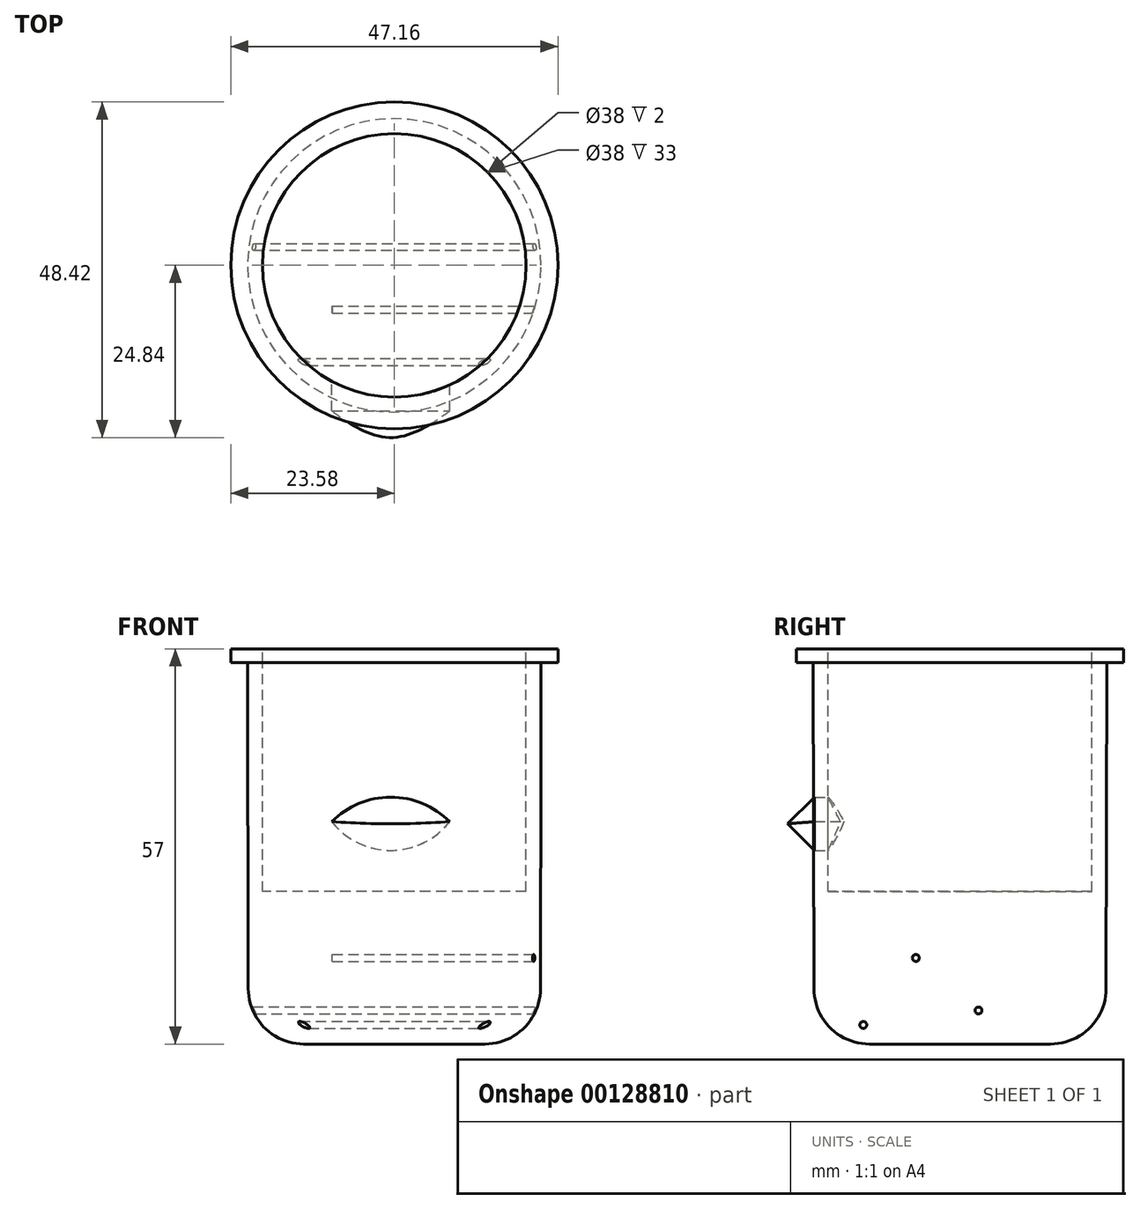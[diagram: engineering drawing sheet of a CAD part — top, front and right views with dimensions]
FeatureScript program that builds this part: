
annotation { "Feature Type Name" : "Feature", "Feature Type Description" : "" }
export const myFeature = defineFeature(function(context is Context, id is Id, definition is map)
    precondition{}
    {
        {
            var Q0;
            Q0=qCreatedBy(makeId("Top.planeOp"),FACE);
            cPlane(context, id + "F0", {"entities" : qUnion([Q0]), "cplaneType" : CPlaneType.OFFSET, "offset" : 55 * mm, "width" : 150 * mm, "height" : 150 * mm});
        }
        {
            var Q0;
            Q0=qCreatedBy(makeId("Top.planeOp"),FACE);
            var sketch = newSketch(context, id + "F1", { "sketchPlane" : qUnion([Q0])});
            skCircle(sketch, "E0", {"center": v(0, 0) * mm, "radius": 21.05 * mm});
            skSolve(sketch);
        }
        {
            var Q0;
            Q0=qCreatedBy(id+"F0.planeOp",FACE);
            var sketch = newSketch(context, id + "F2", { "sketchPlane" : qUnion([Q0])});
            skCircle(sketch, "E1", {"center": v(0, 0) * mm, "radius": 21.16 * mm});
            skSolve(sketch);
        }
        {
            var Q0;
            Q0 = qSketchRegion(id + "F1", true);
            var Q1;
            Q1 = qSketchRegion(id + "F2", true);
            loft(context, id + "F3", {"sheetProfilesArray" : [{ "sheetProfileEntities" : qUnion([Q0]) }, { "sheetProfileEntities" : qUnion([Q1]) }]});
        }
        {
            var Q0;
            Q0=makeQuery(id+"F3.opLoft","CAP_FACE",FACE,{"disambiguationData":[OSD([makeQuery(id+"F1.imprint","IMPRINT",FACE,{"disambiguationData":[TD([[makeQuery(id+"F1.imprint","IMPRINT",EDGE,{"derivedFrom":sQuery(id+"F1.wireOp",EDGE,"E0")}),1.0]])]})])],"isStart":true});
            fillet(context, id + "F4", {"entities" : qUnion([Q0]), "radius" : 8 * mm, "tangentPropagation" : true, "allowEdgeOverflow" : false});
        }
        {
            var Q0;
            Q0=qCreatedBy(makeId("Front.planeOp"),FACE);
            cPlane(context, id + "F5", {"entities" : qUnion([Q0]), "cplaneType" : CPlaneType.OFFSET, "offset" : 21 * mm, "width" : 150 * mm, "height" : 150 * mm});
        }
        {
            var Q0;
            Q0=qCreatedBy(id+"F5.planeOp",FACE);
            var sketch = newSketch(context, id + "F6", { "sketchPlane" : qUnion([Q0])});
            skLineSegment(sketch, "E2", {"start": v(0, 0) * mm, "end": v(0, 27.95) * mm});
            skArc(sketch, "E3", {"start": v(7.97, 32.08) * mm, "mid": v(-0.53, 35.62) * mm, "end": v(-9.03, 32.08) * mm});
            skArc(sketch, "E4", {"start": v(-9.03, 32.08) * mm, "mid": v(-0.53, 27.93) * mm, "end": v(7.97, 32.08) * mm});
            skSolve(sketch);
        }
        {
            var Q0;
            Q0 = qSketchRegion(id + "F6", true);
            extrude(context, id + "F7", {"entities" : qUnion([Q0]), "depth" : 10 * mm, "symmetric" : true});
        }
        {
            var Q0;
            Q0=makeQuery(id+"F7.opExtrude","CAP_EDGE",EDGE,{"disambiguationData":[OSD([sQuery(id+"F6.wireOp",EDGE,"E3")])],"isStart":false});
            chamfer(context, id + "F8", {"entities" : qUnion([Q0]), "chamferType" : ChamferType.TWO_OFFSETS, "width1" : 5 * mm, "oppositeDirection" : false, "width2" : 5 * mm, "tangentPropagation" : true});
        }
        {
            var Q0;
            Q0=makeQuery(id+"F7.opExtrude","CAP_EDGE",EDGE,{"disambiguationData":[OSD([sQuery(id+"F6.wireOp",EDGE,"E4")])],"isStart":false});
            chamfer(context, id + "F9", {"entities" : qUnion([Q0]), "width" : 5 * mm, "tangentPropagation" : true});
        }
        {
            var Q0;
            Q0=qCreatedBy(id+"F0.planeOp",FACE);
            var sketch = newSketch(context, id + "F10", { "sketchPlane" : qUnion([Q0])});
            skCircle(sketch, "E5", {"center": v(0, 0) * mm, "radius": 23.58 * mm});
            skSolve(sketch);
        }
        {
            var Q0;
            Q0 = qSketchRegion(id + "F10", true);
            extrude(context, id + "F11", {"entities" : qUnion([Q0]), "depth" : 2 * mm});
        }
        {
            var Q0;
            Q0=qCreatedBy(id+"F0.planeOp",FACE);
            cPlane(context, id + "F12", {"entities" : qUnion([Q0]), "cplaneType" : CPlaneType.OFFSET, "offset" : 2 * mm, "width" : 150 * mm, "height" : 150 * mm});
        }
        {
            var Q0;
            Q0=qCreatedBy(id+"F12.planeOp",FACE);
            var sketch = newSketch(context, id + "F13", { "sketchPlane" : qUnion([Q0])});
            skCircle(sketch, "E6", {"center": v(0, 0) * mm, "radius": 19 * mm});
            skSolve(sketch);
        }
        {
            var Q0;
            Q0 = qSketchRegion(id + "F13", true);
            extrude(context, id + "F14", {"entities" : qUnion([Q0]), "operationType" : NewBodyOperationType.REMOVE, "oppositeDirection" : true, "depth" : 35 * mm});
        }
        {
            var Q0;
            Q0=qCreatedBy(makeId("Right.planeOp"),FACE);
            cPlane(context, id + "F15", {"entities" : qUnion([Q0]), "cplaneType" : CPlaneType.OFFSET, "offset" : 21 * mm, "width" : 150 * mm, "height" : 150 * mm});
        }
        {
            var Q0;
            Q0=qCreatedBy(id+"F15.planeOp",FACE);
            var sketch = newSketch(context, id + "F16", { "sketchPlane" : qUnion([Q0])});
            skLineSegment(sketch, "E7", {"start": v(2.66, 0) * mm, "end": v(2.66, 4.84) * mm});
            skCircle(sketch, "E8", {"center": v(2.66, 4.84) * mm, "radius": 0.5 * mm});
            skSolve(sketch);
        }
        {
            var Q0;
            Q0 = qSketchRegion(id + "F16", true);
            extrude(context, id + "F17", {"entities" : qUnion([Q0]), "operationType" : NewBodyOperationType.REMOVE, "oppositeDirection" : true, "depth" : 58.07 * mm});
        }
        {
            var Q0;
            Q0=qCreatedBy(id+"F15.planeOp",FACE);
            var sketch = newSketch(context, id + "F18", { "sketchPlane" : qUnion([Q0])});
            skLineSegment(sketch, "E9", {"start": v(3.05, 4.76) * mm, "end": v(-13.95, 4.76) * mm});
            skLineSegment(sketch, "E10", {"start": v(-13.95, 4.76) * mm, "end": v(-13.95, 2.76) * mm});
            skCircle(sketch, "E11", {"center": v(-13.95, 2.76) * mm, "radius": 0.5 * mm});
            skSolve(sketch);
        }
        {
            var Q0;
            Q0 = qSketchRegion(id + "F18", true);
            extrude(context, id + "F19", {"entities" : qUnion([Q0]), "operationType" : NewBodyOperationType.REMOVE, "oppositeDirection" : true, "depth" : 70 * mm});
        }
        {
            var Q0;
            Q0=qCreatedBy(id+"F15.planeOp",FACE);
            var sketch = newSketch(context, id + "F20", { "sketchPlane" : qUnion([Q0])});
            skLineSegment(sketch, "E12", {"start": v(-13.37, 2.86) * mm, "end": v(-6.37, 2.86) * mm});
            skLineSegment(sketch, "E13", {"start": v(-6.37, 2.86) * mm, "end": v(-6.37, 12.43) * mm});
            skCircle(sketch, "E14", {"center": v(-6.37, 12.43) * mm, "radius": 0.5 * mm});
            skSolve(sketch);
        }
        {
            var Q0;
            Q0 = qSketchRegion(id + "F20", true);
            extrude(context, id + "F21", {"entities" : qUnion([Q0]), "operationType" : NewBodyOperationType.REMOVE, "oppositeDirection" : true, "depth" : 29.94 * mm});
        }
        {
            var Q0;
            Q0=qCreatedBy(makeId("Front.planeOp"),FACE);
            cPlane(context, id + "F22", {"entities" : qUnion([Q0]), "cplaneType" : CPlaneType.OFFSET, "offset" : 21 * mm, "oppositeDirection" : true, "width" : 150 * mm, "height" : 150 * mm});
        }
    });
